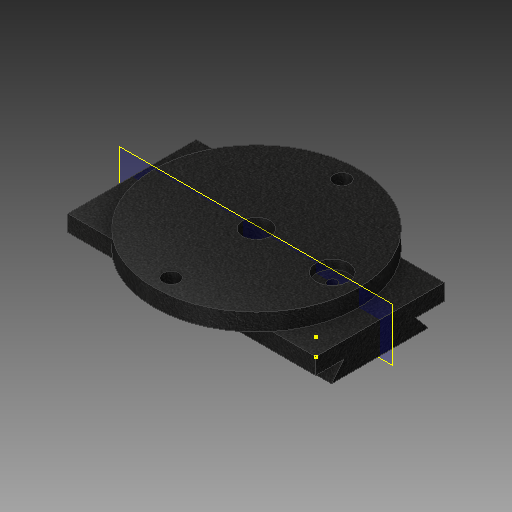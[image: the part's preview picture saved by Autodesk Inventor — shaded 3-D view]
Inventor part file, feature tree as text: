
AUTODESK INVENTOR PART (.ipt)
format: ipt  version: 2018 (Build 220112000, 112)  size: 228,864 bytes
history: native  units: mm
features: sketch x8, extrude x6, plane x1
ambient origin geometry x8: Origin, YZ Plane, XZ Plane, XY Plane, X Axis, Y Axis, Z Axis, Center Point
bodies: Solid1 (feature_tree)
feature tree (15):
  extrude  "Extrusion1"  Depth=19.0mm
  sketch  "Sketch2"  dims[d8=165.2mm d9=0.0mm d10=14.0mm]
  extrude  "Extrusion2"  Depth=165.2mm
  extrude  "Extrusion3"  Depth=11.5mm TaperAngle=0.0deg
  extrude  "Extrusion4"  Depth=73.75mm TaperAngle=0.0deg
  sketch  "Sketch6"  dims[d19=5.4mm d20=5.4mm]
  extrude  "Extrusion5"  Depth=6.0mm
  extrude  "Extrusion6"  Depth=5.4mm
  plane  "Work Plane1"
  sketch  "Sketch1"  dims[d1=85.6mm d7=19.0mm]
  sketch  "Sketch3"  dims[d11=68.3mm d12=11.5mm d13=0.0mm]
  sketch  "Sketch4"  dims[d14=18.3mm d15=73.75mm d16=0.0mm]
  sketch  "Sketch5"  dims[d17=6.0mm d18=6.0mm]
  sketch  "Sketch7"  dims[d21=73.75mm d22=0.0mm]
  sketch  "Sketch8"  dims[d23=6.9mm d24=10.8mm d25=6.0mm d26=0.0mm d27=6.2mm d28=22.8mm d29=0.0mm d30=8.726646mm d31=19.0mm d32=8.726646mm d33=10.0mm]
